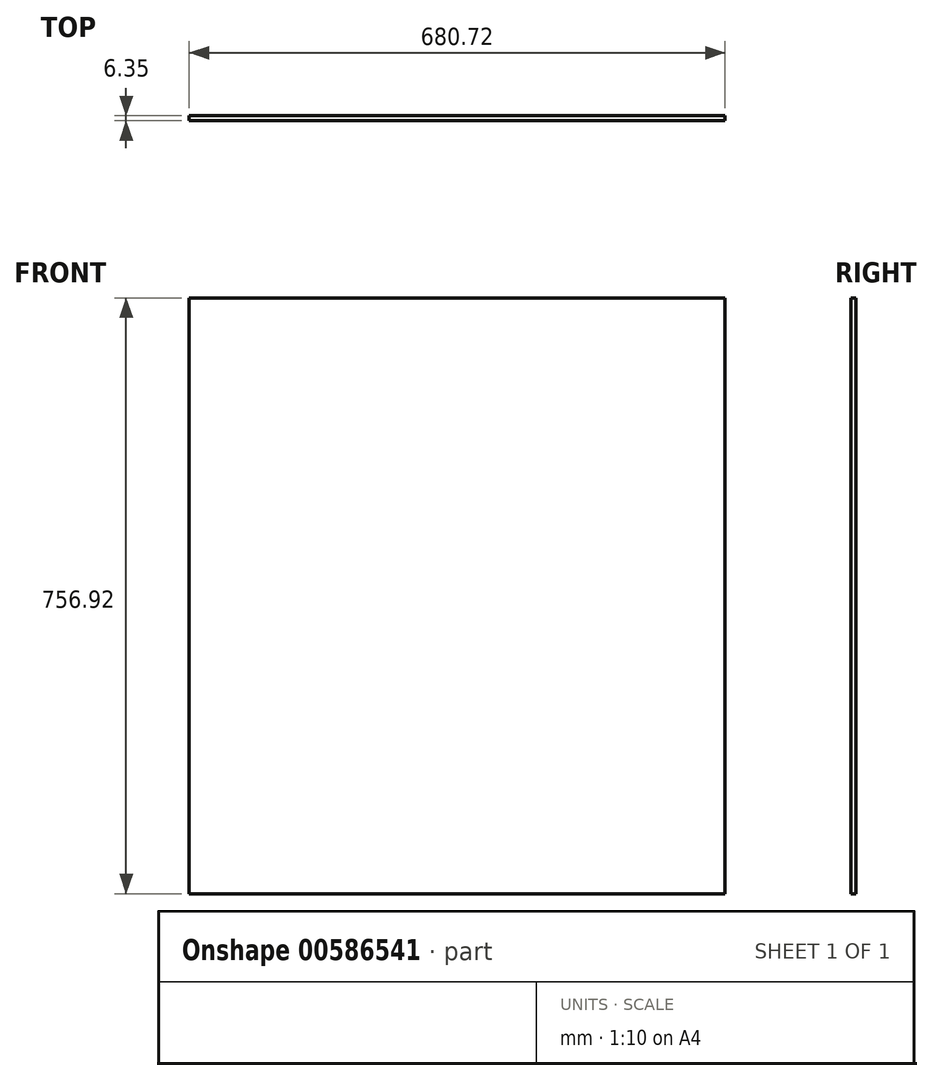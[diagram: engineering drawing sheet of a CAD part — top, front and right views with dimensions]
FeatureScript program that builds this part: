
annotation { "Feature Type Name" : "Feature", "Feature Type Description" : "" }
export const myFeature = defineFeature(function(context is Context, id is Id, definition is map)
    precondition{}
    {
        {
            var Q0;
            Q0=qCreatedBy(makeId("Front.planeOp"),FACE);
            var sketch = newSketch(context, id + "F0", { "sketchPlane" : qUnion([Q0])});
            skLineSegment(sketch, "E0.bottom", {"start": v(-340.36, 378.46) * mm, "end": v(340.36, 378.46) * mm});
            skLineSegment(sketch, "E0.top", {"start": v(-340.36, -378.46) * mm, "end": v(340.36, -378.46) * mm});
            skLineSegment(sketch, "E0.left", {"start": v(-340.36, 378.46) * mm, "end": v(-340.36, -378.46) * mm});
            skLineSegment(sketch, "E0.right", {"start": v(340.36, 378.46) * mm, "end": v(340.36, -378.46) * mm});
            skSolve(sketch);
        }
        {
            var Q0;
            Q0 = qSketchRegion(id + "F0", true);
            extrude(context, id + "F1", {"entities" : qUnion([Q0]), "depth" : 6.35 * mm, "offsetDistance" : 25.4 * mm});
        }
    });
